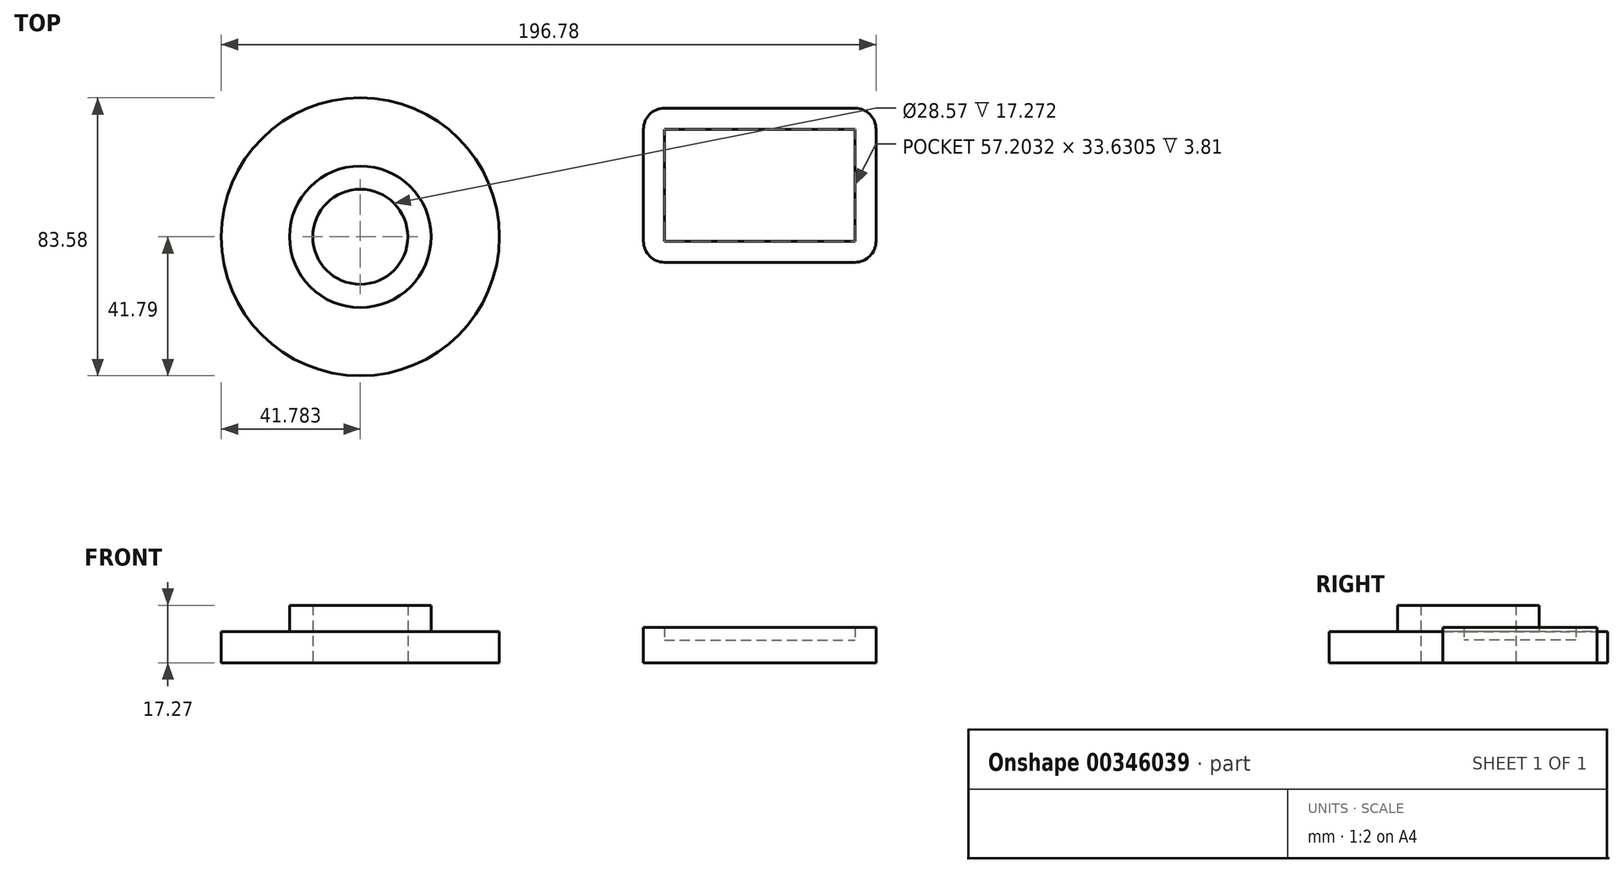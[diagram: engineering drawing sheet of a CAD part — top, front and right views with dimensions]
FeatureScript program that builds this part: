
annotation { "Feature Type Name" : "Feature", "Feature Type Description" : "" }
export const myFeature = defineFeature(function(context is Context, id is Id, definition is map)
    precondition{}
    {
        {
            var Q0;
            Q0=qCreatedBy(makeId("Top.planeOp"),FACE);
            var sketch = newSketch(context, id + "F0", { "sketchPlane" : qUnion([Q0])});
            skCircle(sketch, "E0", {"center": v(-48.46, 0) * mm, "radius": 21.28 * mm});
            skCircle(sketch, "E1", {"center": v(-48.46, 0) * mm, "radius": 14.28 * mm});
            skCircle(sketch, "E2", {"center": v(-48.46, 0) * mm, "radius": 41.79 * mm});
            skSolve(sketch);
        }
        {
            var Q0;
            Q0=makeQuery(id+"F0.imprint","IMPRINT",FACE,{"disambiguationData":[TD([[makeQuery(id+"F0.imprint","IMPRINT",EDGE,{"derivedFrom":sQuery(id+"F0.wireOp",EDGE,"E0")}),-1.0]])]});
            extrude(context, id + "F1", {"entities" : qUnion([Q0]), "depth" : 9.4 * mm});
        }
        {
            var Q0;
            Q0=makeQuery(id+"F0.imprint","IMPRINT",FACE,{"disambiguationData":[TD([[makeQuery(id+"F0.imprint","IMPRINT",EDGE,{"derivedFrom":sQuery(id+"F0.wireOp",EDGE,"E0")}),1.0]])]});
            extrude(context, id + "F2", {"entities" : qUnion([Q0]), "operationType" : NewBodyOperationType.ADD, "depth" : 17.27 * mm});
        }
        {
            var Q0;
            Q0=qCreatedBy(makeId("Top.planeOp"),FACE);
            var sketch = newSketch(context, id + "F3", { "sketchPlane" : qUnion([Q0])});
            skLineSegment(sketch, "E3.bottom", {"start": v(42.99, 38.66) * mm, "end": v(100.2, 38.66) * mm});
            skLineSegment(sketch, "E3.top", {"start": v(42.99, -7.67) * mm, "end": v(100.2, -7.67) * mm});
            skLineSegment(sketch, "E3.left", {"start": v(36.64, 32.31) * mm, "end": v(36.64, -1.32) * mm});
            skLineSegment(sketch, "E3.right", {"start": v(106.54, 32.31) * mm, "end": v(106.54, -1.32) * mm});
            skPoint(sketch, "E4.visualSharp", {"position": v(36.64, 38.66) * mm});
            skArc(sketch, "E4.filletArc", {"start": v(42.99, 38.66) * mm, "mid": v(38.5, 36.8) * mm, "end": v(36.64, 32.31) * mm});
            skPoint(sketch, "E5.visualSharp", {"position": v(106.54, 38.66) * mm});
            skArc(sketch, "E5.filletArc", {"start": v(106.54, 32.31) * mm, "mid": v(104.68, 36.8) * mm, "end": v(100.2, 38.66) * mm});
            skPoint(sketch, "E6.visualSharp", {"position": v(106.54, -7.67) * mm});
            skArc(sketch, "E6.filletArc", {"start": v(100.2, -7.67) * mm, "mid": v(104.68, -5.8) * mm, "end": v(106.54, -1.32) * mm});
            skPoint(sketch, "E7.visualSharp", {"position": v(36.64, -7.67) * mm});
            skArc(sketch, "E7.filletArc", {"start": v(36.64, -1.32) * mm, "mid": v(38.5, -5.8) * mm, "end": v(42.99, -7.67) * mm});
            skLineSegment(sketch, "E8.bottom", {"start": v(42.99, 32.31) * mm, "end": v(100.2, 32.31) * mm});
            skLineSegment(sketch, "E8.top", {"start": v(42.99, -1.32) * mm, "end": v(100.2, -1.32) * mm});
            skLineSegment(sketch, "E8.left", {"start": v(42.99, 32.31) * mm, "end": v(42.99, -1.32) * mm});
            skLineSegment(sketch, "E8.right", {"start": v(100.2, 32.31) * mm, "end": v(100.2, -1.32) * mm});
            skSolve(sketch);
        }
        {
            var Q0;
            Q0=makeQuery(id+"F3.imprint","IMPRINT",FACE,{"disambiguationData":[TD([[makeQuery(id+"F3.imprint","IMPRINT",EDGE,{"derivedFrom":sQuery(id+"F3.wireOp",EDGE,"E3.bottom")}),-1.0]])]});
            extrude(context, id + "F4", {"entities" : qUnion([Q0]), "depth" : 10.67 * mm});
        }
        {
            var Q0;
            Q0=makeQuery(id+"F3.imprint","IMPRINT",FACE,{"disambiguationData":[TD([[makeQuery(id+"F3.imprint","IMPRINT",EDGE,{"derivedFrom":sQuery(id+"F3.wireOp",EDGE,"E3.bottom")}),-1.0]])]});
            var Q1;
            Q1=makeQuery(id+"F3.imprint","IMPRINT",FACE,{"disambiguationData":[TD([[makeQuery(id+"F3.imprint","IMPRINT",EDGE,{"derivedFrom":sQuery(id+"F3.wireOp",EDGE,"E8.bottom")}),-1.0]])]});
            extrude(context, id + "F5", {"entities" : qUnion([Q0, Q1]), "operationType" : NewBodyOperationType.ADD, "depth" : 6.86 * mm});
        }
    });
